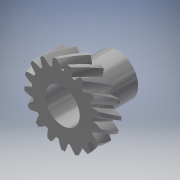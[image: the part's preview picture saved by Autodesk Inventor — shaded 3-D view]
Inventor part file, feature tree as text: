
AUTODESK INVENTOR PART (.ipt)
format: ipt  version: 2017 (Build 210142000, 142)  size: 512,000 bytes
history: native  units: mm (DEFAULTED — no unit token found)
features: sketch x5, extrude x4, plane x3, other x3, projected_geometry x1
ambient origin geometry x8: Origin, YZ Plane, XZ Plane, XY Plane, X Axis, Y Axis, Z Axis, Center Point
bodies: Solid1 (feature_tree)
feature tree (16):
  extrude  "Extrusion1"  Depth=10.16mm TaperAngle=0.0deg
  plane  "Work Plane1"
  plane  "Work Plane2"
  plane  "Work Plane3"
  other  "Spur Gear"
  extrude  "Extrusion2"  Depth=76.2mm TaperAngle=0.0deg
  extrude  "Extrusion3"  TaperAngle=0.0deg  [1 undecoded]
  extrude  "Extrusion4"  TaperAngle=0.0deg  [1 undecoded]
  sketch  "Sketch1"  dims[d0=14.176796mm d1=10.16mm d2=0.0mm]
  sketch  "Sketch2"  dims[d3=12.552326mm d4=76.2mm d5=0.0mm]
  other  "Srf1"
  sketch  "Sketch3"  dims[d6=0.0mm d7=1.847996mm d9=0.0mm]
  sketch  "Sketch4"  dims[d14=0.0mm d15=31.75mm d16=0.0mm]
  projected_geometry  "Projected Loop1"
  sketch  "Sketch5"  dims[d17=0.0mm d18=0.0mm d19=31.75mm d20=6.096mm d21=25.4mm d22=0.0mm d23=8.89mm d24=6.35mm d25=0.0mm d26=2.54mm d27=6.35mm d28=0.0mm]
  other  "Pitch Diameter"
note: 2 required parameter values undecoded (feature->parameter linkage not recoverable at this tier; creation-order binding heuristic only, values carry confidence <= 0.55)
